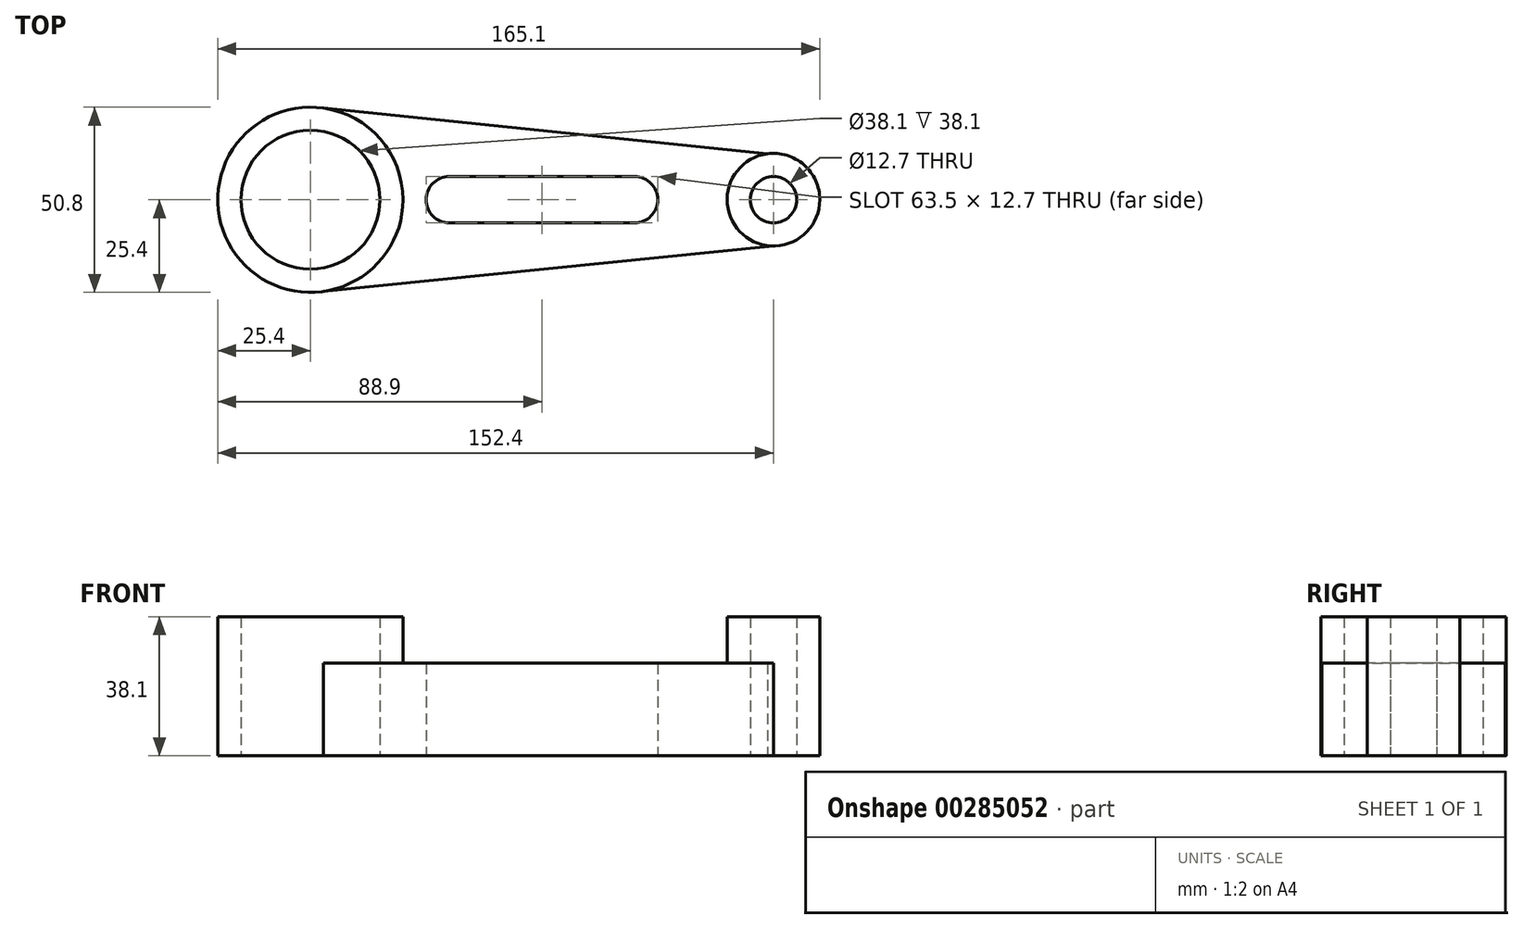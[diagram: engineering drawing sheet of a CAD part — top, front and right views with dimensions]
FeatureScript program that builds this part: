
annotation { "Feature Type Name" : "Feature", "Feature Type Description" : "" }
export const myFeature = defineFeature(function(context is Context, id is Id, definition is map)
    precondition{}
    {
        {
            var Q0;
            Q0=qCreatedBy(makeId("Top.planeOp"),FACE);
            var sketch = newSketch(context, id + "F0", { "sketchPlane" : qUnion([Q0])});
            skCircle(sketch, "E0", {"center": v(0, 0) * mm, "radius": 19.05 * mm});
            skCircle(sketch, "E1", {"center": v(0, 0) * mm, "radius": 25.4 * mm});
            skCircle(sketch, "E2", {"center": v(127, 0) * mm, "radius": 6.35 * mm});
            skCircle(sketch, "E3", {"center": v(127, 0) * mm, "radius": 12.7 * mm});
            skLineSegment(sketch, "E4", {"start": v(3.6, 25.14) * mm, "end": v(125.32, 12.59) * mm});
            skLineSegment(sketch, "E5", {"start": v(3.6, -25.14) * mm, "end": v(127, -12.7) * mm});
            skArc(sketch, "E6", {"start": v(38.1, 6.35) * mm, "mid": v(31.75, 0) * mm, "end": v(38.1, -6.35) * mm});
            skArc(sketch, "E7", {"start": v(88.9, -6.35) * mm, "mid": v(95.25, 0) * mm, "end": v(88.9, 6.35) * mm});
            skLineSegment(sketch, "E8", {"start": v(38.1, 6.35) * mm, "end": v(88.9, 6.35) * mm});
            skLineSegment(sketch, "E9", {"start": v(38.1, -6.35) * mm, "end": v(88.9, -6.35) * mm});
            skSolve(sketch);
        }
        {
            var Q0;
            {var subQ0=sQuery(id+"F0.wireOp",EDGE,"E4");Q0=makeQuery(id+"F0.imprint","IMPRINT",FACE,{"disambiguationData":[TD([[makeQuery(id+"F0.imprint","IMPRINT",EDGE,{"derivedFrom":subQ0}),-1.0]])]});}
            extrude(context, id + "F1", {"entities" : qUnion([Q0]), "depth" : 25.4 * mm});
        }
        {
            var Q0;
            Q0=makeQuery(id+"F0.imprint","IMPRINT",FACE,{"disambiguationData":[TD([[makeQuery(id+"F0.imprint","IMPRINT",EDGE,{"derivedFrom":sQuery(id+"F0.wireOp",EDGE,"E0")}),-1.0]])]});
            var Q1;
            Q1=makeQuery(id+"F0.imprint","IMPRINT",FACE,{"disambiguationData":[TD([[makeQuery(id+"F0.imprint","IMPRINT",EDGE,{"derivedFrom":sQuery(id+"F0.wireOp",EDGE,"E2")}),-1.0]])]});
            extrude(context, id + "F2", {"entities" : qUnion([Q0, Q1]), "operationType" : NewBodyOperationType.ADD, "depth" : 38.1 * mm});
        }
    });
